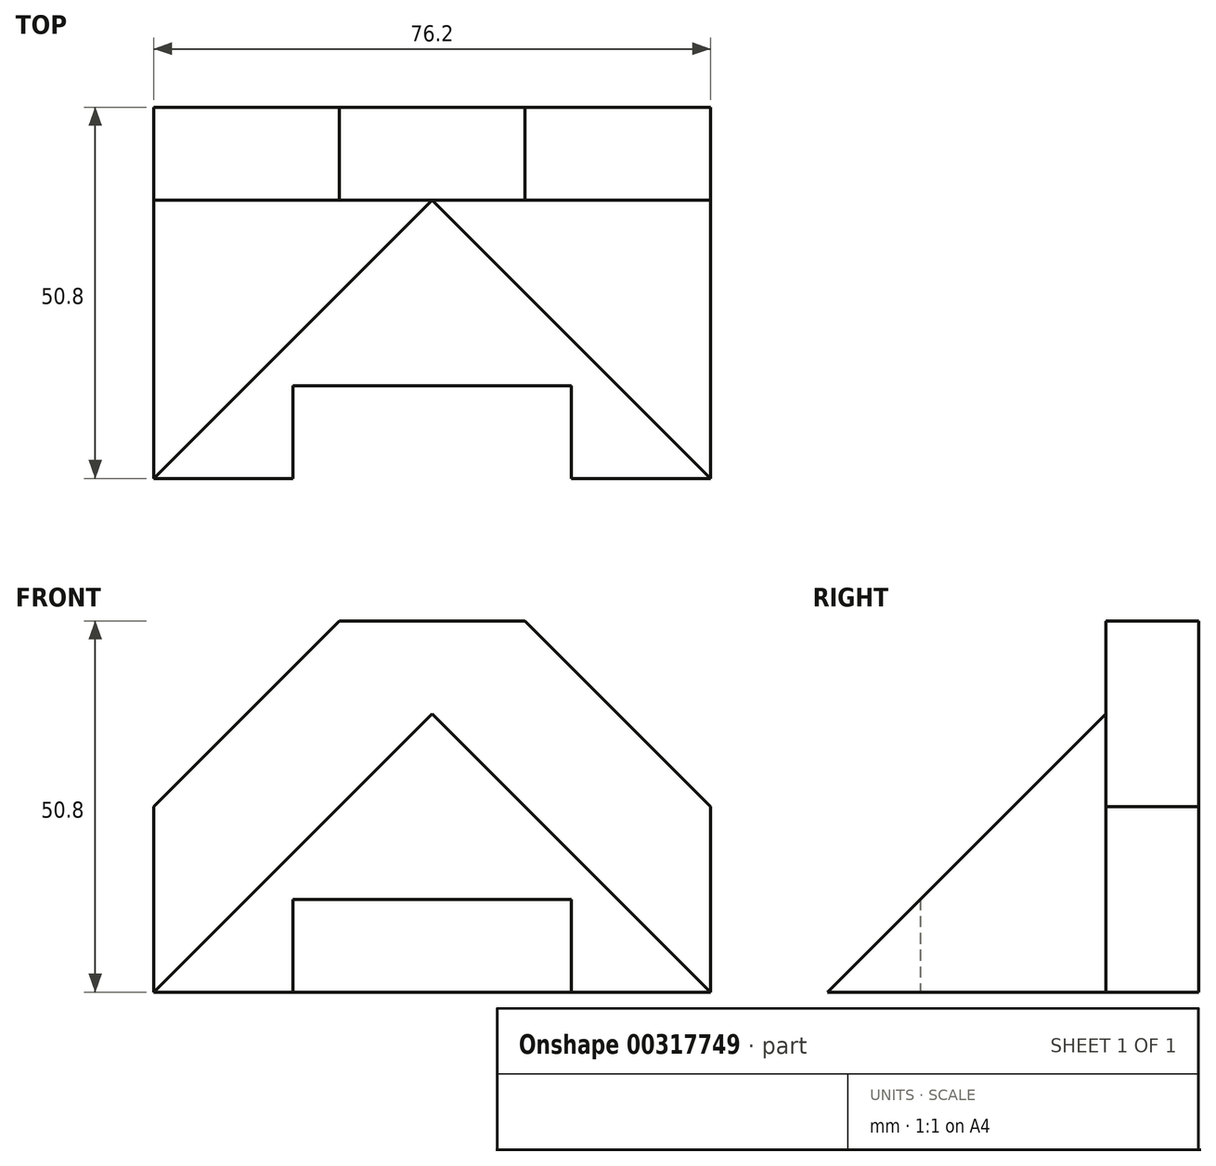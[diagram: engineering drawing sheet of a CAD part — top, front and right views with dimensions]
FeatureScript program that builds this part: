
annotation { "Feature Type Name" : "Feature", "Feature Type Description" : "" }
export const myFeature = defineFeature(function(context is Context, id is Id, definition is map)
    precondition{}
    {
        {
            var Q0;
            Q0=qCreatedBy(makeId("Right.planeOp"),FACE);
            var sketch = newSketch(context, id + "F0", { "sketchPlane" : qUnion([Q0])});
            skLineSegment(sketch, "E0", {"start": v(0, 0) * mm, "end": v(38.1, 38.1) * mm});
            skLineSegment(sketch, "E1", {"start": v(38.1, 38.1) * mm, "end": v(38.1, 50.8) * mm});
            skLineSegment(sketch, "E2", {"start": v(38.1, 50.8) * mm, "end": v(50.8, 50.8) * mm});
            skLineSegment(sketch, "E3", {"start": v(50.8, 50.8) * mm, "end": v(50.8, 0) * mm});
            skLineSegment(sketch, "E4", {"start": v(50.8, 0) * mm, "end": v(0, 0) * mm});
            skSolve(sketch);
        }
        {
            var Q0;
            Q0=makeQuery(id+"F0.imprint","IMPRINT",FACE,{"disambiguationData":[TD([[makeQuery(id+"F0.imprint","IMPRINT",EDGE,{"derivedFrom":sQuery(id+"F0.wireOp",EDGE,"E0")}),-1.0]])]});
            extrude(context, id + "F1", {"entities" : qUnion([Q0]), "depth" : 76.2 * mm});
        }
        {
            var Q0;
            Q0=makeQuery(id+"F1.opExtrude","SWEPT_FACE",FACE,{"disambiguationData":[OSD([sQuery(id+"F0.wireOp",EDGE,"E3")])]});
            var sketch = newSketch(context, id + "F2", { "sketchPlane" : qUnion([Q0])});
            skLineSegment(sketch, "E5", {"start": v(-38.1, 38.1) * mm, "end": v(-76.2, 0) * mm});
            skLineSegment(sketch, "E6", {"start": v(0, 0) * mm, "end": v(-38.1, 38.1) * mm});
            skLineSegment(sketch, "E7", {"start": v(-38.1, 38.1) * mm, "end": v(0, 38.1) * mm});
            skLineSegment(sketch, "E8", {"start": v(0, 38.1) * mm, "end": v(0, 0) * mm});
            skLineSegment(sketch, "E9", {"start": v(-38.1, 38.1) * mm, "end": v(-76.2, 38.1) * mm});
            skLineSegment(sketch, "E10", {"start": v(-76.2, 38.1) * mm, "end": v(-76.2, 0) * mm});
            skSolve(sketch);
        }
        {
            var Q0;
            Q0=makeQuery(id+"F2.imprint","IMPRINT",FACE,{"disambiguationData":[TD([[makeQuery(id+"F2.imprint","IMPRINT",EDGE,{"derivedFrom":sQuery(id+"F2.wireOp",EDGE,"E5")}),-1.0]])]});
            var Q1;
            Q1=makeQuery(id+"F2.imprint","IMPRINT",FACE,{"disambiguationData":[TD([[makeQuery(id+"F2.imprint","IMPRINT",EDGE,{"derivedFrom":sQuery(id+"F2.wireOp",EDGE,"E6")}),-1.0]])]});
            extrude(context, id + "F3", {"entities" : qUnion([Q0, Q1]), "operationType" : NewBodyOperationType.REMOVE, "endBound" : BoundingType.THROUGH_ALL, "oppositeDirection" : true, "depth" : 25.4 * mm, "hasSecondDirection" : true, "secondDirectionOppositeDirection" : true, "secondDirectionDepth" : 12.7 * mm});
        }
        {
            var Q0;
            Q0=makeQuery(id+"F3.boolean.opBoolean","MERGE",FACE,{"derivedFrom":[makeQuery(id+"F1.opExtrude","SWEPT_FACE",FACE,{"disambiguationData":[OSD([sQuery(id+"F0.wireOp",EDGE,"E1")])]}),makeQuery(id+"F3.opExtrude","CAP_FACE",FACE,{"disambiguationData":[OSD([sQuery(id+"F2.wireOp",EDGE,"E5"),sQuery(id+"F2.wireOp",EDGE,"E9"),sQuery(id+"F2.wireOp",EDGE,"E10")])],"isStart":true}),makeQuery(id+"F3.opExtrude","CAP_FACE",FACE,{"disambiguationData":[OSD([sQuery(id+"F2.wireOp",EDGE,"E6"),sQuery(id+"F2.wireOp",EDGE,"E7"),sQuery(id+"F2.wireOp",EDGE,"E8")])],"isStart":true})]});
            var sketch = newSketch(context, id + "F4", { "sketchPlane" : qUnion([Q0])});
            skLineSegment(sketch, "E11", {"start": v(25.4, 50.8) * mm, "end": v(0, 25.4) * mm});
            skLineSegment(sketch, "E12", {"start": v(0, 25.4) * mm, "end": v(0, 50.8) * mm});
            skLineSegment(sketch, "E13", {"start": v(0, 50.8) * mm, "end": v(25.4, 50.8) * mm});
            skLineSegment(sketch, "E14", {"start": v(76.2, 50.8) * mm, "end": v(76.2, 25.4) * mm});
            skLineSegment(sketch, "E15", {"start": v(76.2, 25.4) * mm, "end": v(50.8, 50.8) * mm});
            skLineSegment(sketch, "E16", {"start": v(50.8, 50.8) * mm, "end": v(76.2, 50.8) * mm});
            skSolve(sketch);
        }
        {
            var Q0;
            Q0=makeQuery(id+"F4.imprint","IMPRINT",FACE,{"disambiguationData":[TD([[makeQuery(id+"F4.imprint","IMPRINT",EDGE,{"derivedFrom":sQuery(id+"F4.wireOp",EDGE,"E11")}),-1.0]])]});
            var Q1;
            Q1=makeQuery(id+"F4.imprint","IMPRINT",FACE,{"disambiguationData":[TD([[makeQuery(id+"F4.imprint","IMPRINT",EDGE,{"derivedFrom":sQuery(id+"F4.wireOp",EDGE,"E14")}),1.0]])]});
            extrude(context, id + "F5", {"entities" : qUnion([Q0, Q1]), "operationType" : NewBodyOperationType.REMOVE, "endBound" : BoundingType.THROUGH_ALL, "oppositeDirection" : true, "depth" : 25.4 * mm});
        }
        {
            var Q0;
            Q0=makeQuery(id+"F1.opExtrude","SWEPT_FACE",FACE,{"disambiguationData":[OSD([sQuery(id+"F0.wireOp",EDGE,"E4")])]});
            var sketch = newSketch(context, id + "F6", { "sketchPlane" : qUnion([Q0])});
            skLineSegment(sketch, "E17.bottom", {"start": v(19.05, 0) * mm, "end": v(57.15, 0) * mm});
            skLineSegment(sketch, "E17.top", {"start": v(19.05, -12.7) * mm, "end": v(57.15, -12.7) * mm});
            skLineSegment(sketch, "E17.left", {"start": v(19.05, 0) * mm, "end": v(19.05, -12.7) * mm});
            skLineSegment(sketch, "E17.right", {"start": v(57.15, 0) * mm, "end": v(57.15, -12.7) * mm});
            skSolve(sketch);
        }
        {
            var Q0;
            Q0=makeQuery(id+"F6.imprint","IMPRINT",FACE,{"disambiguationData":[TD([[makeQuery(id+"F6.imprint","IMPRINT",EDGE,{"derivedFrom":sQuery(id+"F6.wireOp",EDGE,"E17.bottom")}),1.0]])]});
            extrude(context, id + "F7", {"entities" : qUnion([Q0]), "operationType" : NewBodyOperationType.REMOVE, "endBound" : BoundingType.THROUGH_ALL, "oppositeDirection" : true, "depth" : 25.4 * mm});
        }
    });
